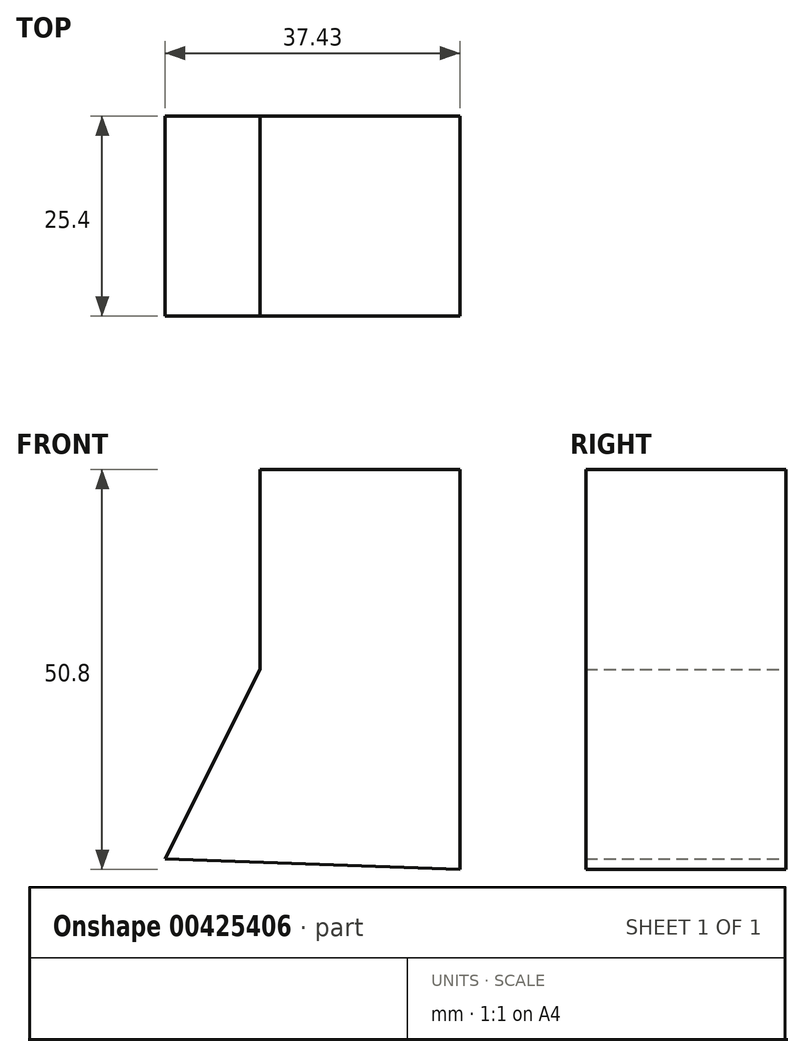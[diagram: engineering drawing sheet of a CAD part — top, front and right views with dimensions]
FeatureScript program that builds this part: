
annotation { "Feature Type Name" : "Feature", "Feature Type Description" : "" }
export const myFeature = defineFeature(function(context is Context, id is Id, definition is map)
    precondition{}
    {
        {
            var Q0;
            Q0=qCreatedBy(makeId("Front.planeOp"),FACE);
            var sketch = newSketch(context, id + "F0", { "sketchPlane" : qUnion([Q0])});
            skLineSegment(sketch, "E0", {"start": v(-47.55, 53.28) * mm, "end": v(-22.15, 53.28) * mm});
            skLineSegment(sketch, "E1", {"start": v(-47.55, 53.28) * mm, "end": v(-47.55, 27.88) * mm});
            skLineSegment(sketch, "E2", {"start": v(-22.15, 53.28) * mm, "end": v(-22.15, 2.48) * mm});
            skLineSegment(sketch, "E3", {"start": v(-47.55, 27.88) * mm, "end": v(-59.58, 3.82) * mm});
            skLineSegment(sketch, "E4", {"start": v(-22.15, 2.48) * mm, "end": v(-59.58, 3.82) * mm});
            skSolve(sketch);
        }
        {
            var Q0;
            Q0 = qSketchRegion(id + "F0", true);
            extrude(context, id + "F1", {"entities" : qUnion([Q0]), "depth" : 25.4 * mm});
        }
    });
